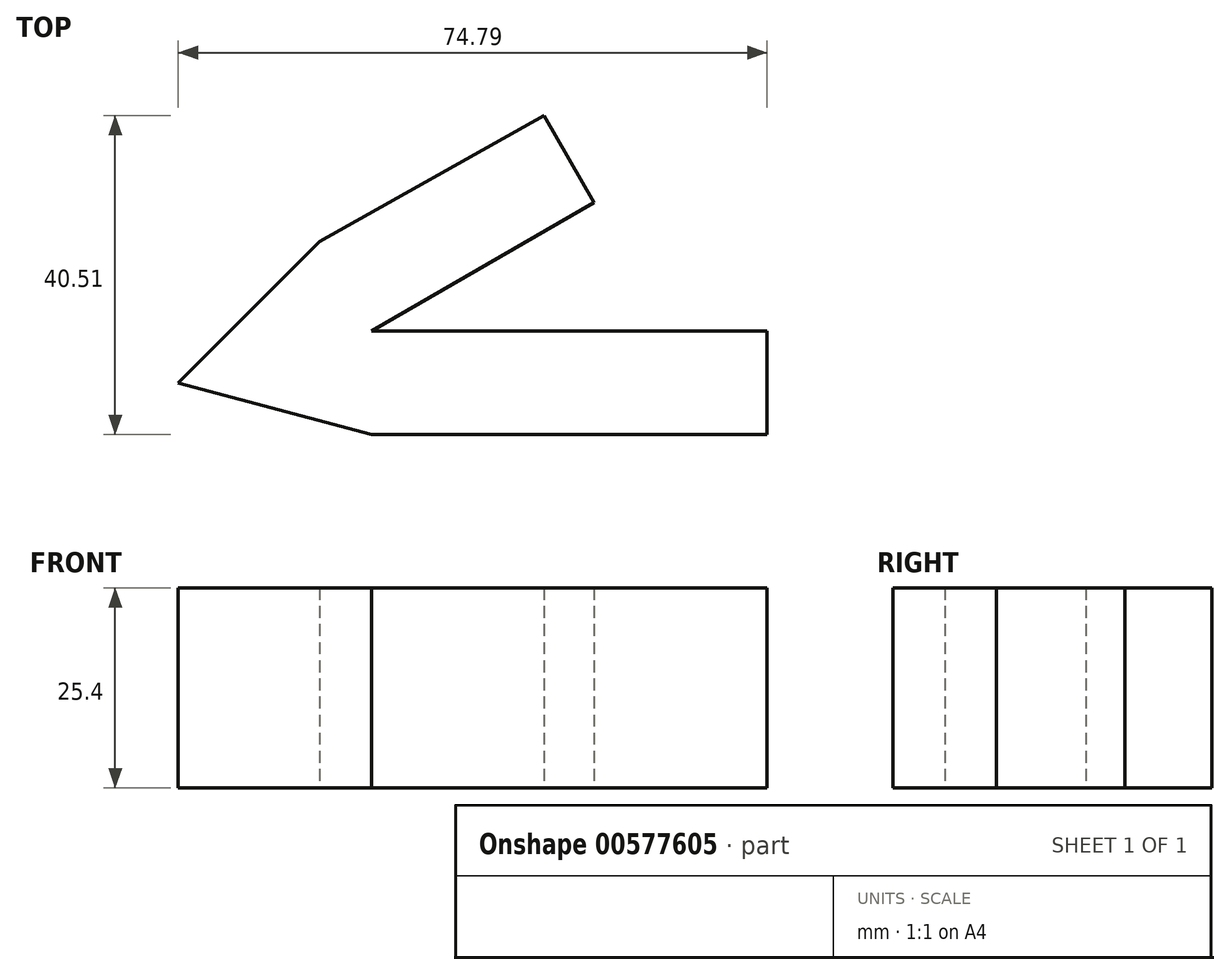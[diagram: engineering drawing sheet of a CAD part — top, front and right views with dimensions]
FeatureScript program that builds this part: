
annotation { "Feature Type Name" : "Feature", "Feature Type Description" : "" }
export const myFeature = defineFeature(function(context is Context, id is Id, definition is map)
    precondition{}
    {
        {
            var Q0;
            Q0=qCreatedBy(makeId("Top.planeOp"),FACE);
            var sketch = newSketch(context, id + "F0", { "sketchPlane" : qUnion([Q0])});
            skLineSegment(sketch, "E0", {"start": v(-47.67, 0) * mm, "end": v(-23.14, 6.57) * mm});
            skLineSegment(sketch, "E1", {"start": v(-23.14, 6.57) * mm, "end": v(27.12, 6.57) * mm});
            skLineSegment(sketch, "E2", {"start": v(27.12, 6.57) * mm, "end": v(27.12, -6.57) * mm});
            skLineSegment(sketch, "E3", {"start": v(27.12, -6.57) * mm, "end": v(-23.14, -6.57) * mm});
            skLineSegment(sketch, "E4", {"start": v(-23.14, -6.57) * mm, "end": v(-47.67, 0) * mm});
            skLineSegment(sketch, "E5", {"start": v(-47.67, 0) * mm, "end": v(-29.71, 17.96) * mm});
            skLineSegment(sketch, "E6", {"start": v(-23.14, 6.57) * mm, "end": v(5.15, 22.9) * mm});
            skLineSegment(sketch, "E7", {"start": v(5.15, 22.9) * mm, "end": v(-1.22, 33.94) * mm});
            skLineSegment(sketch, "E8", {"start": v(-1.22, 33.94) * mm, "end": v(-29.71, 17.96) * mm});
            skSolve(sketch);
        }
        {
            var Q0;
            Q0=makeQuery(id+"F0.imprint","IMPRINT",FACE,{"disambiguationData":[TD([[makeQuery(id+"F0.imprint","IMPRINT",EDGE,{"derivedFrom":sQuery(id+"F0.wireOp",EDGE,"E0")}),1.0]])]});
            var Q1;
            Q1=makeQuery(id+"F0.imprint","IMPRINT",FACE,{"disambiguationData":[TD([[makeQuery(id+"F0.imprint","IMPRINT",EDGE,{"derivedFrom":sQuery(id+"F0.wireOp",EDGE,"E0")}),-1.0]])]});
            extrude(context, id + "F1", {"entities" : qUnion([Q0, Q1]), "depth" : 25.4 * mm, "offsetDistance" : 25.4 * mm});
        }
    });
